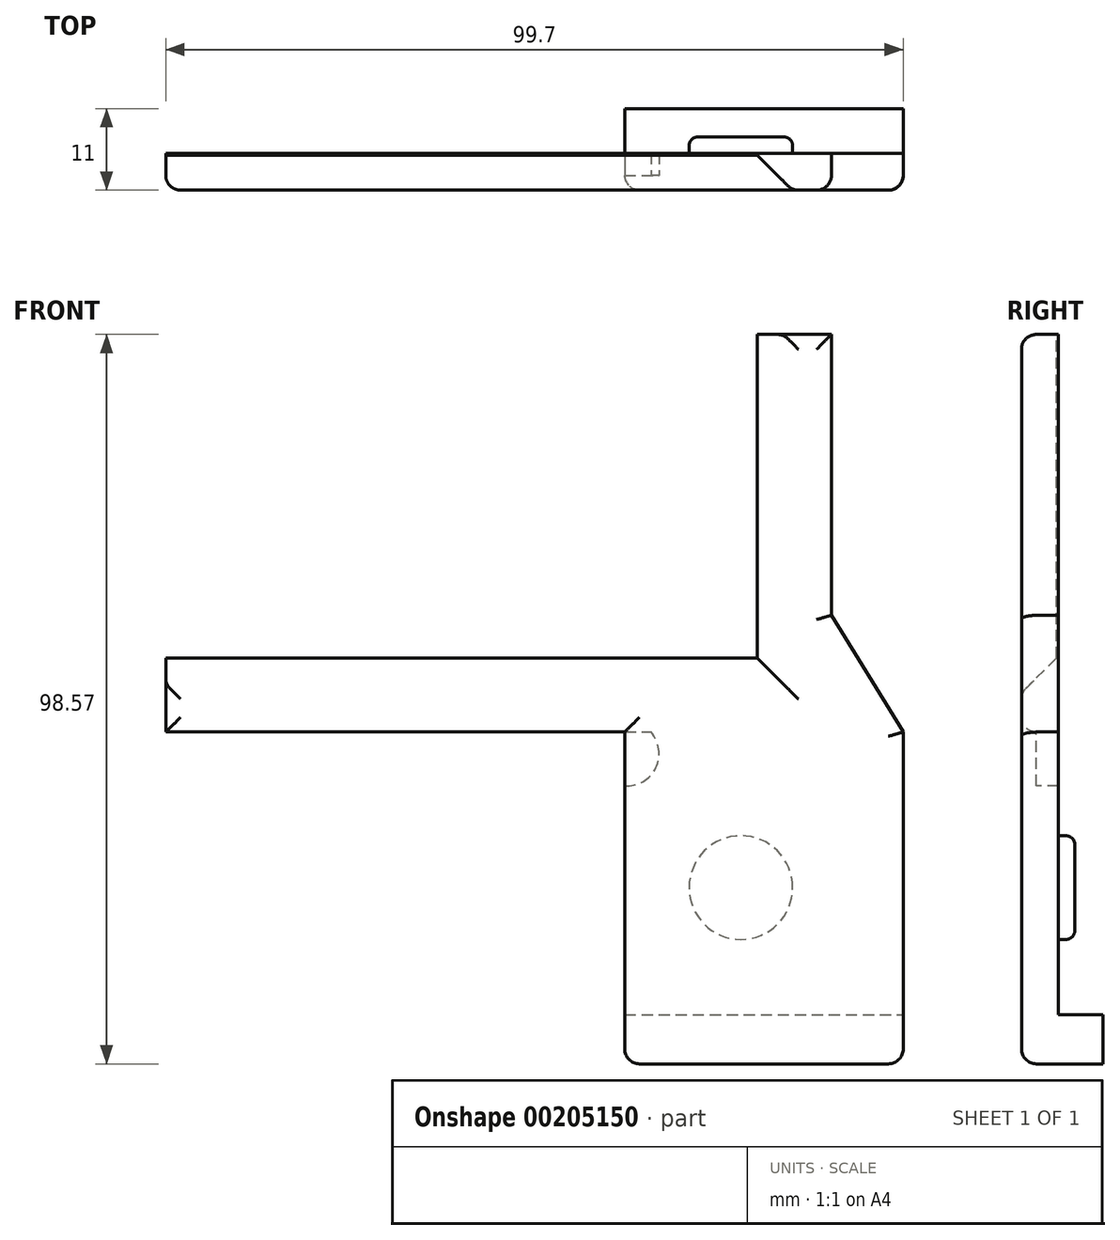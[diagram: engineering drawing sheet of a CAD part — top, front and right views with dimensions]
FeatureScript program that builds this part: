
annotation { "Feature Type Name" : "Feature", "Feature Type Description" : "" }
export const myFeature = defineFeature(function(context is Context, id is Id, definition is map)
    precondition{}
    {
        {
            var Q0;
            Q0=qCreatedBy(makeId("Front.planeOp"),FACE);
            var sketch = newSketch(context, id + "F0", { "sketchPlane" : qUnion([Q0])});
            skCircle(sketch, "E0", {"center": v(34.83, -44.48) * mm, "radius": 7 * mm});
            skLineSegment(sketch, "E1.bottom", {"start": v(19.12, -61.68) * mm, "end": v(56.77, -61.68) * mm});
            skLineSegment(sketch, "E1.top", {"start": v(19.12, -68.3) * mm, "end": v(56.77, -68.3) * mm});
            skLineSegment(sketch, "E1.left", {"start": v(19.12, -61.68) * mm, "end": v(19.12, -68.3) * mm});
            skLineSegment(sketch, "E1.right", {"start": v(56.77, -61.68) * mm, "end": v(56.77, -68.3) * mm});
            skLineSegment(sketch, "E2.bottom", {"start": v(-42.93, -13.46) * mm, "end": v(37.07, -13.46) * mm});
            skLineSegment(sketch, "E2.top", {"start": v(-42.93, -23.46) * mm, "end": v(37.07, -23.46) * mm});
            skLineSegment(sketch, "E2.left", {"start": v(-42.93, -13.46) * mm, "end": v(-42.93, -23.46) * mm});
            skLineSegment(sketch, "E2.right", {"start": v(37.07, -13.46) * mm, "end": v(37.07, -23.46) * mm});
            skLineSegment(sketch, "E3.bottom", {"start": v(37.07, 30.27) * mm, "end": v(47.07, 30.27) * mm});
            skLineSegment(sketch, "E3.top", {"start": v(37.07, -23.46) * mm, "end": v(47.07, -23.46) * mm});
            skLineSegment(sketch, "E3.left", {"start": v(47.07, 30.27) * mm, "end": v(47.07, -23.46) * mm});
            skLineSegment(sketch, "E3.right", {"start": v(37.07, 30.27) * mm, "end": v(37.07, -23.46) * mm});
            skLineSegment(sketch, "E4.top", {"start": v(19.12, -23.46) * mm, "end": v(56.77, -23.46) * mm});
            skLineSegment(sketch, "E4.left", {"start": v(19.12, -61.68) * mm, "end": v(19.12, -23.46) * mm});
            skLineSegment(sketch, "E4.right", {"start": v(56.77, -61.68) * mm, "end": v(56.77, -23.46) * mm});
            skLineSegment(sketch, "E5", {"start": v(47.07, -7.69) * mm, "end": v(56.77, -23.46) * mm});
            skSolve(sketch);
        }
        {
            var Q0;
            Q0=makeQuery(id+"F0.imprint","IMPRINT",FACE,{"disambiguationData":[TD([[makeQuery(id+"F0.imprint","IMPRINT",EDGE,{"derivedFrom":sQuery(id+"F0.wireOp",EDGE,"E1.top")}),1.0]])]});
            extrude(context, id + "F1", {"entities" : qUnion([Q0]), "oppositeDirection" : true, "depth" : 6 * mm, "hasSecondDirection" : true, "secondDirectionOppositeDirection" : false, "secondDirectionDepth" : 5 * mm});
        }
        {
            var Q0;
            Q0=makeQuery(id+"F0.imprint","IMPRINT",FACE,{"disambiguationData":[TD([[makeQuery(id+"F0.imprint","IMPRINT",EDGE,{"derivedFrom":sQuery(id+"F0.wireOp",EDGE,"E0")}),1.0]])]});
            var Q1;
            Q1=makeQuery(id+"F0.imprint","IMPRINT",FACE,{"disambiguationData":[TD([[makeQuery(id+"F0.imprint","IMPRINT",EDGE,{"derivedFrom":sQuery(id+"F0.wireOp",EDGE,"E0")}),-1.0]])]});
            var Q2;
            {var subQ2=sQuery(id+"F0.wireOp",EDGE,"E3.bottom");Q2=makeQuery(id+"F0.imprint","IMPRINT",FACE,{"disambiguationData":[TD([[makeQuery(id+"F0.imprint","IMPRINT",EDGE,{"derivedFrom":subQ2}),-1.0]])]});}
            var Q3;
            {var subQ3=sQuery(id+"F0.wireOp",EDGE,"E5");Q3=makeQuery(id+"F0.imprint","IMPRINT",FACE,{"disambiguationData":[TD([[makeQuery(id+"F0.imprint","IMPRINT",EDGE,{"derivedFrom":subQ3}),-1.0]])]});}
            var Q4;
            {var subQ1=sQuery(id+"F0.wireOp",EDGE,"E2.bottom");Q4=makeQuery(id+"F0.imprint","IMPRINT",FACE,{"disambiguationData":[TD([[makeQuery(id+"F0.imprint","IMPRINT",EDGE,{"derivedFrom":subQ1}),-1.0]])]});}
            extrude(context, id + "F2", {"entities" : qUnion([Q0, Q1, Q2, Q3, Q4]), "operationType" : NewBodyOperationType.ADD, "depth" : 5 * mm});
        }
        {
            var Q0;
            Q0=makeQuery(id+"F0.imprint","IMPRINT",FACE,{"disambiguationData":[TD([[makeQuery(id+"F0.imprint","IMPRINT",EDGE,{"derivedFrom":sQuery(id+"F0.wireOp",EDGE,"E0")}),1.0]])]});
            extrude(context, id + "F3", {"entities" : qUnion([Q0]), "operationType" : NewBodyOperationType.ADD, "oppositeDirection" : true, "depth" : 2.2 * mm});
        }
        {
            var Q0;
            Q0=makeQuery(id+"F2.opExtrude","CAP_EDGE",EDGE,{"disambiguationData":[OSD([sQuery(id+"F0.wireOp",EDGE,"E2.bottom")])],"isStart":false});
            var Q1;
            Q1=makeQuery(id+"F2.opExtrude","CAP_EDGE",EDGE,{"disambiguationData":[OSD([sQuery(id+"F0.wireOp",EDGE,"E3.right")])],"isStart":false});
            chamfer(context, id + "F4", {"entities" : qUnion([Q0, Q1]), "width" : 4.7 * mm, "tangentPropagation" : true});
        }
        {
            var Q0;
            Q0=makeQuery(id+"F3.opExtrude","CAP_FACE",FACE,{"disambiguationData":[OSD([sQuery(id+"F0.wireOp",EDGE,"E0")])],"isStart":false});
            fillet(context, id + "F5", {"entities" : qUnion([Q0]), "radius" : 1.2 * mm, "tangentPropagation" : true, "allowEdgeOverflow" : false});
        }
        {
            var Q0;
            Q0=makeQuery(id+"F2.opExtrude","CAP_EDGE",EDGE,{"disambiguationData":[OSD([sQuery(id+"F0.wireOp",EDGE,"E5")])],"isStart":false});
            var Q1;
            Q1=makeQuery(id+"F2.opExtrude","CAP_EDGE",EDGE,{"disambiguationData":[OSD([sQuery(id+"F0.wireOp",EDGE,"E3.left")])],"isStart":false});
            var Q2;
            Q2=makeQuery(id+"F2.boolean.opBoolean","MERGE",EDGE,{"derivedFrom":[makeQuery(id+"F1.opExtrude","CAP_EDGE",EDGE,{"disambiguationData":[OSD([sQuery(id+"F0.wireOp",EDGE,"E1.right")])],"isStart":true}),makeQuery(id+"F2.opExtrude","CAP_EDGE",EDGE,{"disambiguationData":[OSD([sQuery(id+"F0.wireOp",EDGE,"E4.right")])],"isStart":false})]});
            var Q3;
            Q3=makeQuery(id+"F1.opExtrude","CAP_EDGE",EDGE,{"disambiguationData":[OSD([sQuery(id+"F0.wireOp",EDGE,"E1.top")])],"isStart":true});
            var Q4;
            {var subQ0=sQuery(id+"F0.wireOp",EDGE,"E1.bottom");Q4=makeQuery(id+"F2.boolean.opBoolean","MERGE",FACE,{"derivedFrom":[makeQuery(id+"F1.opExtrude","CAP_FACE",FACE,{"disambiguationData":[OSD([sQuery(id+"F0.wireOp",EDGE,"E1.top"),sQuery(id+"F0.wireOp",EDGE,"E1.left"),sQuery(id+"F0.wireOp",EDGE,"E1.right"),subQ0])],"isStart":true}),makeQuery(id+"F2.opExtrude","CAP_FACE",FACE,{"disambiguationData":[OSD([sQuery(id+"F0.wireOp",EDGE,"E2.bottom"),sQuery(id+"F0.wireOp",EDGE,"E2.top"),sQuery(id+"F0.wireOp",EDGE,"E2.left"),sQuery(id+"F0.wireOp",EDGE,"E3.bottom"),sQuery(id+"F0.wireOp",EDGE,"E3.left"),sQuery(id+"F0.wireOp",EDGE,"E3.right"),subQ0,sQuery(id+"F0.wireOp",EDGE,"E4.left"),sQuery(id+"F0.wireOp",EDGE,"E4.right"),sQuery(id+"F0.wireOp",EDGE,"E5")])],"isStart":false})]});}
            var Q5;
            Q5=makeQuery(id+"F1.opExtrude","SWEPT_EDGE",EDGE,{"disambiguationData":[OSD([sQuery(id+"F0.wireOp",EDGE,"E1.top"),sQuery(id+"F0.wireOp",EDGE,"E1.left")])]});
            var Q6;
            Q6=makeQuery(id+"F1.opExtrude","SWEPT_EDGE",EDGE,{"disambiguationData":[OSD([sQuery(id+"F0.wireOp",EDGE,"E1.top"),sQuery(id+"F0.wireOp",EDGE,"E1.right")])]});
            fillet(context, id + "F6", {"entities" : qUnion([Q0, Q1, Q2, Q3, Q4, Q5, Q6]), "radius" : 2 * mm, "tangentPropagation" : true, "allowEdgeOverflow" : false});
        }
        {
            var Q0;
            Q0=makeQuery(id+"F0.imprint","IMPRINT",FACE,{"disambiguationData":[TD([[makeQuery(id+"F0.imprint","IMPRINT",EDGE,{"derivedFrom":sQuery(id+"F0.wireOp",EDGE,"E0")}),-1.0]])]});
            var sketch = newSketch(context, id + "F7", { "sketchPlane" : qUnion([Q0])});
            skCircle(sketch, "E6", {"center": v(19.4, -26.37) * mm, "radius": 4.37 * mm});
            skSolve(sketch);
        }
        {
            var Q0;
            {var subQ0=sQuery(id+"F7.wireOp",EDGE,"E6");var subQ1=sQuery(id+"F0.wireOp",EDGE,"E4.left");var subQ5=makeQuery(id+"F0.imprint","IMPRINT",EDGE,{"derivedFrom":subQ1});var subQ6=makeQuery(id+"F7.imprint","INTERSECT",VERTEX,{"derivedFrom":[subQ5,subQ0]});Q0=makeQuery(id+"F7.imprint","IMPRINT",FACE,{"disambiguationData":[TD([[makeQuery(id+"F7.imprint","IMPRINT",EDGE,{"disambiguationData":[TD([[subQ6,-1.0]])],"derivedFrom":subQ0}),1.0]])]});}
            extrude(context, id + "F8", {"entities" : qUnion([Q0]), "operationType" : NewBodyOperationType.REMOVE, "oppositeDirection" : true, "depth" : 2 * mm, "hasSecondDirection" : true, "secondDirectionOppositeDirection" : false, "secondDirectionDepth" : 3 * mm});
        }
    });
